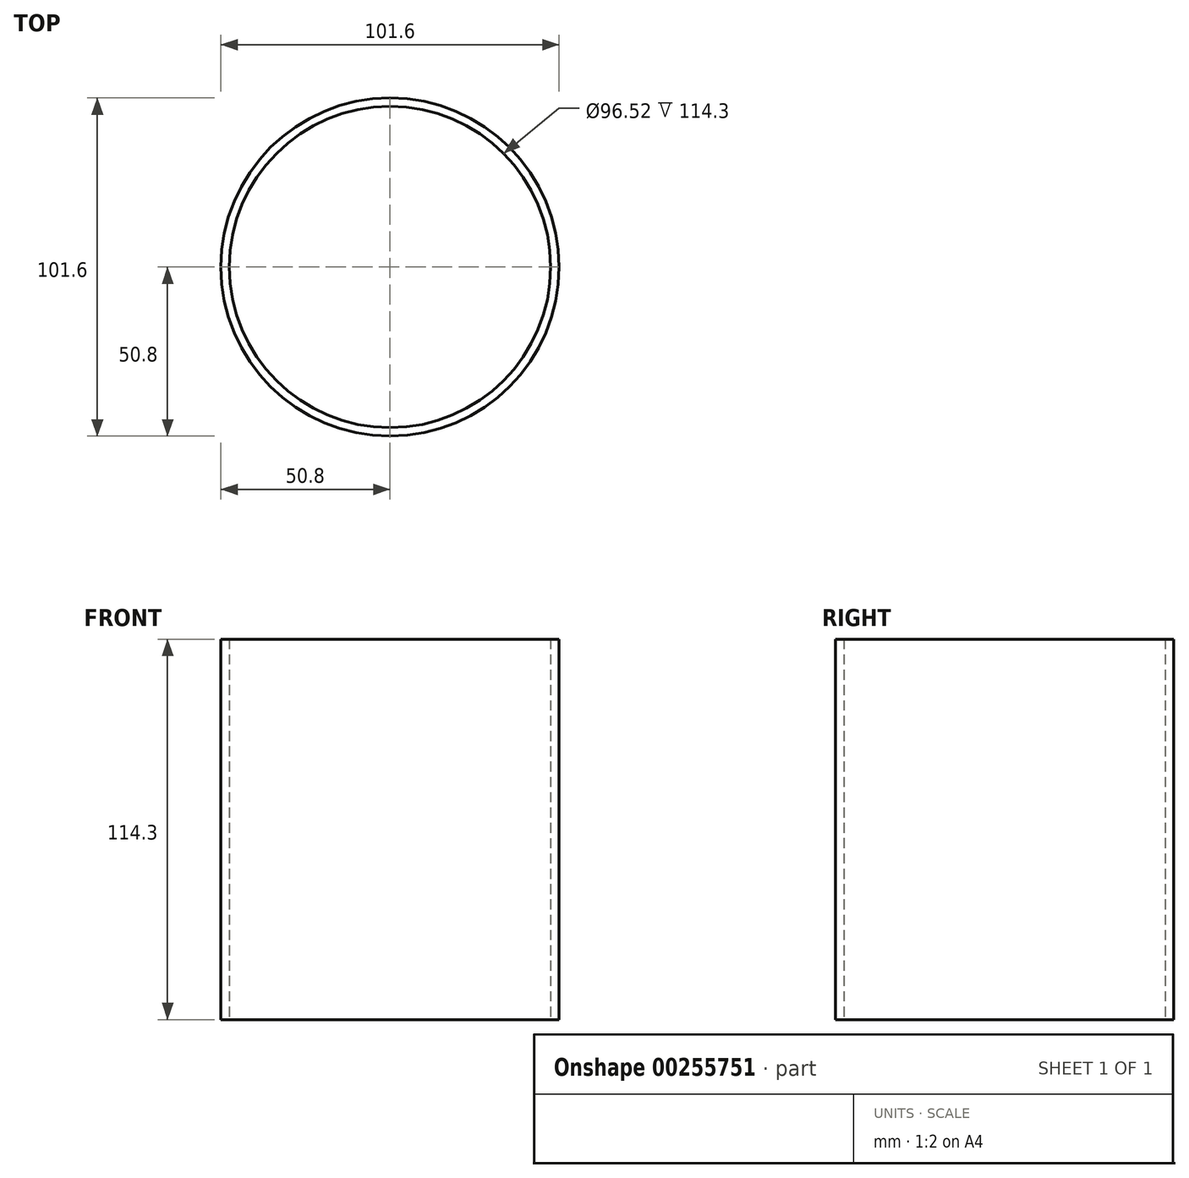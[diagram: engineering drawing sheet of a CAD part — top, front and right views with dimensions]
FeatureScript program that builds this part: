
annotation { "Feature Type Name" : "Feature", "Feature Type Description" : "" }
export const myFeature = defineFeature(function(context is Context, id is Id, definition is map)
    precondition{}
    {
        {
            var Q0;
            Q0=qCreatedBy(makeId("Top.planeOp"),FACE);
            var sketch = newSketch(context, id + "F0", { "sketchPlane" : qUnion([Q0])});
            skCircle(sketch, "E0", {"center": v(0, 0) * mm, "radius": 50.8 * mm});
            skCircle(sketch, "E1", {"center": v(0, 0) * mm, "radius": 48.26 * mm});
            skSolve(sketch);
        }
        {
            var Q0;
            Q0 = qSketchRegion(id + "F0", true);
            extrude(context, id + "F1", {"entities" : qUnion([Q0]), "depth" : 114.3 * mm});
        }
    });
